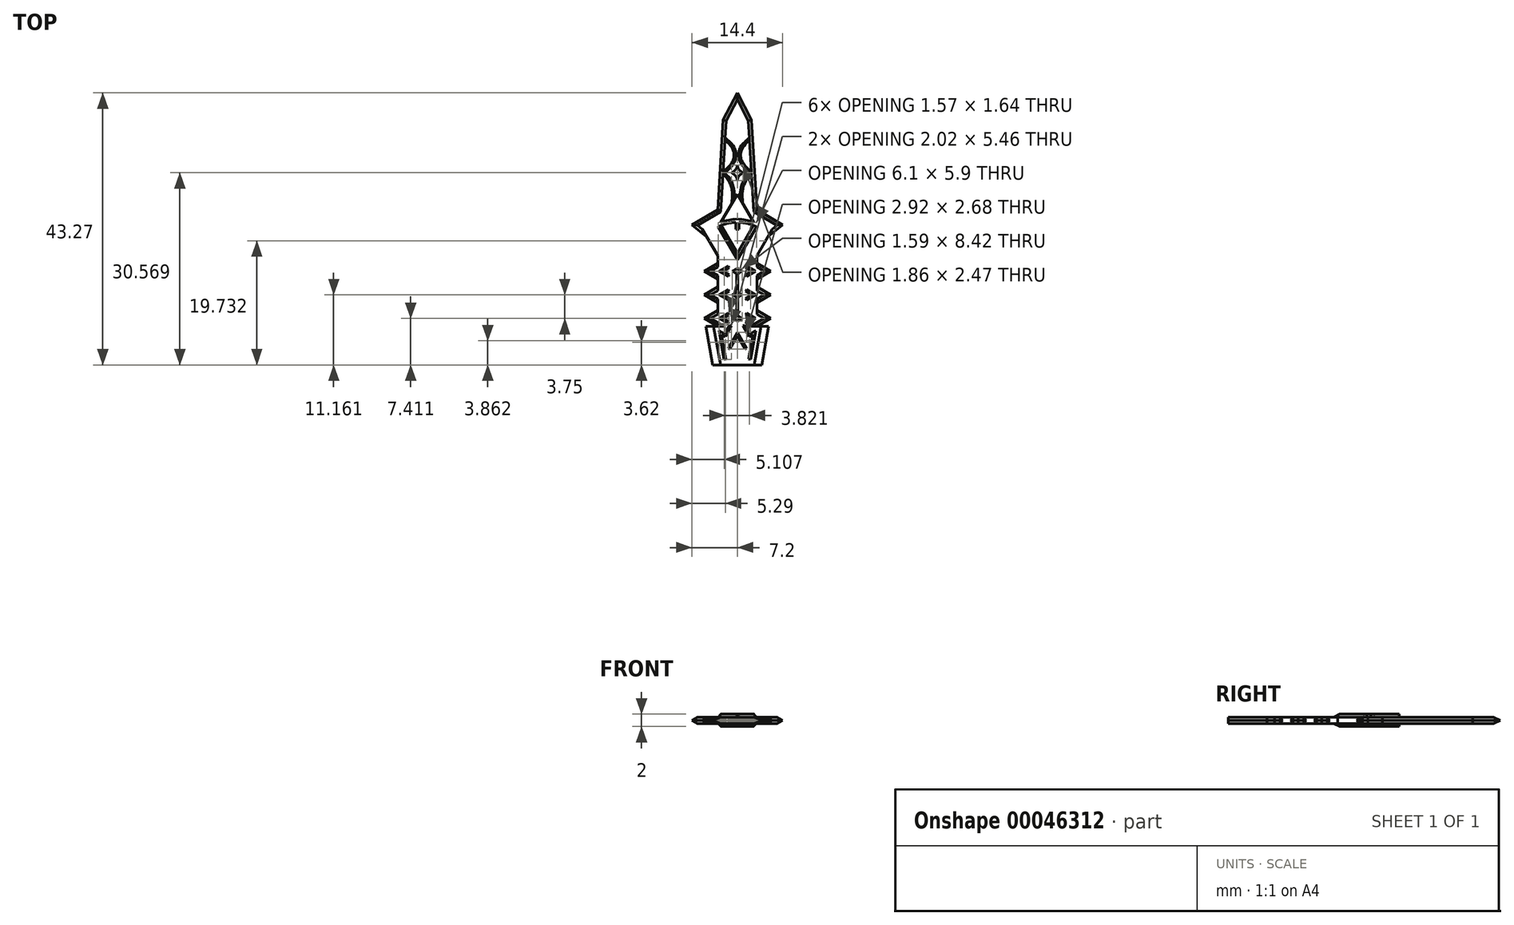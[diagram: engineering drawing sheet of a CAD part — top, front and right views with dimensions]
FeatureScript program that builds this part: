
annotation { "Feature Type Name" : "Feature", "Feature Type Description" : "" }
export const myFeature = defineFeature(function(context is Context, id is Id, definition is map)
    precondition{}
    {
        {
            var Q0;
            Q0=qCreatedBy(makeId("Top.planeOp"),FACE);
            var sketch = newSketch(context, id + "F0", { "sketchPlane" : qUnion([Q0])});
            skLineSegment(sketch, "E0", {"start": v(0, 43.81) * mm, "end": v(-2.25, 39.5) * mm});
            skLineSegment(sketch, "E1", {"start": v(-2.25, 39.5) * mm, "end": v(-3.12, 25.23) * mm});
            skLineSegment(sketch, "E2", {"start": v(-3.12, 25.23) * mm, "end": v(-7.2, 22.8) * mm});
            skLineSegment(sketch, "E3", {"start": v(-7.2, 22.8) * mm, "end": v(-4.87, 20.94) * mm});
            skLineSegment(sketch, "E4", {"start": v(-4.87, 20.94) * mm, "end": v(-3.12, 17.95) * mm});
            skLineSegment(sketch, "E5", {"start": v(-3.12, 17.95) * mm, "end": v(-3.12, 16.7) * mm});
            skLineSegment(sketch, "E6", {"start": v(-3.12, 16.7) * mm, "end": v(-5.28, 15.45) * mm});
            skLineSegment(sketch, "E7", {"start": v(-5.28, 15.45) * mm, "end": v(-3.12, 14.2) * mm});
            skLineSegment(sketch, "E8", {"start": v(-3.12, 14.2) * mm, "end": v(-3.12, 12.95) * mm});
            skLineSegment(sketch, "E9", {"start": v(-3.12, 12.95) * mm, "end": v(-5.28, 11.7) * mm});
            skLineSegment(sketch, "E10", {"start": v(-5.28, 11.7) * mm, "end": v(-3.12, 10.45) * mm});
            skLineSegment(sketch, "E11", {"start": v(-3.12, 10.45) * mm, "end": v(-3.12, 9.2) * mm});
            skLineSegment(sketch, "E12", {"start": v(-3.12, 9.2) * mm, "end": v(-5.28, 7.95) * mm});
            skLineSegment(sketch, "E13", {"start": v(-5.28, 7.95) * mm, "end": v(-3.12, 6.7) * mm});
            skLineSegment(sketch, "E14", {"start": v(-3.12, 6.7) * mm, "end": v(-5.28, 6.7) * mm});
            skLineSegment(sketch, "E15", {"start": v(-5.28, 6.7) * mm, "end": v(-4.2, 0.54) * mm});
            skPoint(sketch, "E15.endSnap0", {"position": v(-4.2, 6.7) * mm});
            skLineSegment(sketch, "E16", {"start": v(-4.2, 0.54) * mm, "end": v(0, 0.54) * mm});
            skLineSegment(sketch, "E17.MirrorCS", {"start": v(3.12, 17.95) * mm, "end": v(3.12, 16.7) * mm});
            skLineSegment(sketch, "E18.MirrorCS", {"start": v(4.87, 20.94) * mm, "end": v(3.12, 17.95) * mm});
            skLineSegment(sketch, "E19.MirrorCS", {"start": v(3.12, 16.7) * mm, "end": v(5.28, 15.45) * mm});
            skLineSegment(sketch, "E20.MirrorCS", {"start": v(5.28, 15.45) * mm, "end": v(3.12, 14.2) * mm});
            skLineSegment(sketch, "E21.MirrorCS", {"start": v(3.12, 14.2) * mm, "end": v(3.12, 12.95) * mm});
            skLineSegment(sketch, "E22.MirrorCS", {"start": v(3.12, 12.95) * mm, "end": v(5.28, 11.7) * mm});
            skLineSegment(sketch, "E23.MirrorCS", {"start": v(5.28, 11.7) * mm, "end": v(3.12, 10.45) * mm});
            skLineSegment(sketch, "E24.MirrorCS", {"start": v(3.12, 10.45) * mm, "end": v(3.12, 9.2) * mm});
            skLineSegment(sketch, "E25.MirrorCS", {"start": v(3.12, 9.2) * mm, "end": v(5.28, 7.95) * mm});
            skLineSegment(sketch, "E26.MirrorCS", {"start": v(5.28, 7.95) * mm, "end": v(3.12, 6.7) * mm});
            skLineSegment(sketch, "E27.MirrorCS", {"start": v(3.12, 6.7) * mm, "end": v(5.28, 6.7) * mm});
            skLineSegment(sketch, "E28.MirrorCS", {"start": v(5.28, 6.7) * mm, "end": v(4.2, 0.54) * mm});
            skLineSegment(sketch, "E29.MirrorCS", {"start": v(0, 43.81) * mm, "end": v(2.25, 39.5) * mm});
            skLineSegment(sketch, "E30.MirrorCS", {"start": v(3.12, 25.23) * mm, "end": v(7.2, 22.8) * mm});
            skLineSegment(sketch, "E31.MirrorCS", {"start": v(7.2, 22.8) * mm, "end": v(4.87, 20.94) * mm});
            skPoint(sketch, "E32.MirrorP", {"position": v(4.2, 6.7) * mm});
            skLineSegment(sketch, "E33.MirrorCS", {"start": v(4.2, 0.54) * mm, "end": v(0, 0.54) * mm});
            skLineSegment(sketch, "E34.MirrorCS", {"start": v(2.25, 39.5) * mm, "end": v(3.12, 25.23) * mm});
            skSolve(sketch);
        }
        {
            var Q0;
            Q0=makeQuery(id+"F0.imprint","IMPRINT",FACE,{"disambiguationData":[TD([[makeQuery(id+"F0.imprint","IMPRINT",EDGE,{"derivedFrom":sQuery(id+"F0.wireOp",EDGE,"E0")}),1.0]])]});
            extrude(context, id + "F1", {"entities" : qUnion([Q0]), "depth" : 0.5 * mm, "hasSecondDirection" : true, "secondDirectionOppositeDirection" : true, "secondDirectionDepth" : 0.5 * mm});
        }
        {
            var Q0;
            Q0=makeQuery(id+"F1.opExtrude","CAP_EDGE",EDGE,{"disambiguationData":[OSD([sQuery(id+"F0.wireOp",EDGE,"E34.MirrorCS")])],"isStart":false});
            var Q1;
            Q1=makeQuery(id+"F1.opExtrude","CAP_EDGE",EDGE,{"disambiguationData":[OSD([sQuery(id+"F0.wireOp",EDGE,"E34.MirrorCS")])],"isStart":true});
            var Q2;
            Q2=makeQuery(id+"F1.opExtrude","CAP_EDGE",EDGE,{"disambiguationData":[OSD([sQuery(id+"F0.wireOp",EDGE,"E29.MirrorCS")])],"isStart":false});
            var Q3;
            Q3=makeQuery(id+"F1.opExtrude","CAP_EDGE",EDGE,{"disambiguationData":[OSD([sQuery(id+"F0.wireOp",EDGE,"E29.MirrorCS")])],"isStart":true});
            var Q4;
            Q4=makeQuery(id+"F1.opExtrude","CAP_EDGE",EDGE,{"disambiguationData":[OSD([sQuery(id+"F0.wireOp",EDGE,"E0")])],"isStart":false});
            var Q5;
            Q5=makeQuery(id+"F1.opExtrude","CAP_EDGE",EDGE,{"disambiguationData":[OSD([sQuery(id+"F0.wireOp",EDGE,"E0")])],"isStart":true});
            var Q6;
            Q6=makeQuery(id+"F1.opExtrude","CAP_EDGE",EDGE,{"disambiguationData":[OSD([sQuery(id+"F0.wireOp",EDGE,"E1")])],"isStart":false});
            var Q7;
            Q7=makeQuery(id+"F1.opExtrude","CAP_EDGE",EDGE,{"disambiguationData":[OSD([sQuery(id+"F0.wireOp",EDGE,"E1")])],"isStart":true});
            var Q8;
            Q8=makeQuery(id+"F1.opExtrude","CAP_EDGE",EDGE,{"disambiguationData":[OSD([sQuery(id+"F0.wireOp",EDGE,"E30.MirrorCS")])],"isStart":true});
            var Q9;
            Q9=makeQuery(id+"F1.opExtrude","CAP_EDGE",EDGE,{"disambiguationData":[OSD([sQuery(id+"F0.wireOp",EDGE,"E30.MirrorCS")])],"isStart":false});
            var Q10;
            Q10=makeQuery(id+"F1.opExtrude","CAP_EDGE",EDGE,{"disambiguationData":[OSD([sQuery(id+"F0.wireOp",EDGE,"E31.MirrorCS")])],"isStart":true});
            var Q11;
            Q11=makeQuery(id+"F1.opExtrude","CAP_EDGE",EDGE,{"disambiguationData":[OSD([sQuery(id+"F0.wireOp",EDGE,"E31.MirrorCS")])],"isStart":false});
            var Q12;
            Q12=makeQuery(id+"F1.opExtrude","CAP_EDGE",EDGE,{"disambiguationData":[OSD([sQuery(id+"F0.wireOp",EDGE,"E2")])],"isStart":false});
            var Q13;
            Q13=makeQuery(id+"F1.opExtrude","CAP_EDGE",EDGE,{"disambiguationData":[OSD([sQuery(id+"F0.wireOp",EDGE,"E2")])],"isStart":true});
            var Q14;
            Q14=makeQuery(id+"F1.opExtrude","CAP_EDGE",EDGE,{"disambiguationData":[OSD([sQuery(id+"F0.wireOp",EDGE,"E3")])],"isStart":false});
            var Q15;
            Q15=makeQuery(id+"F1.opExtrude","CAP_EDGE",EDGE,{"disambiguationData":[OSD([sQuery(id+"F0.wireOp",EDGE,"E3")])],"isStart":true});
            chamfer(context, id + "F2", {"entities" : qUnion([Q0, Q1, Q2, Q3, Q4, Q5, Q6, Q7, Q8, Q9, Q10, Q11, Q12, Q13, Q14, Q15]), "width" : 0.5 * mm, "tangentPropagation" : true});
        }
        {
            var Q0;
            Q0=makeQuery(id+"F1.opExtrude","CAP_EDGE",EDGE,{"disambiguationData":[OSD([sQuery(id+"F0.wireOp",EDGE,"E6")])],"isStart":false});
            var Q1;
            Q1=makeQuery(id+"F1.opExtrude","CAP_EDGE",EDGE,{"disambiguationData":[OSD([sQuery(id+"F0.wireOp",EDGE,"E7")])],"isStart":false});
            var Q2;
            Q2=makeQuery(id+"F1.opExtrude","CAP_EDGE",EDGE,{"disambiguationData":[OSD([sQuery(id+"F0.wireOp",EDGE,"E9")])],"isStart":false});
            var Q3;
            Q3=makeQuery(id+"F1.opExtrude","CAP_EDGE",EDGE,{"disambiguationData":[OSD([sQuery(id+"F0.wireOp",EDGE,"E10")])],"isStart":false});
            var Q4;
            Q4=makeQuery(id+"F1.opExtrude","CAP_EDGE",EDGE,{"disambiguationData":[OSD([sQuery(id+"F0.wireOp",EDGE,"E12")])],"isStart":false});
            var Q5;
            Q5=makeQuery(id+"F1.opExtrude","CAP_EDGE",EDGE,{"disambiguationData":[OSD([sQuery(id+"F0.wireOp",EDGE,"E13")])],"isStart":false});
            var Q6;
            Q6=makeQuery(id+"F1.opExtrude","CAP_EDGE",EDGE,{"disambiguationData":[OSD([sQuery(id+"F0.wireOp",EDGE,"E6")])],"isStart":true});
            var Q7;
            Q7=makeQuery(id+"F1.opExtrude","CAP_EDGE",EDGE,{"disambiguationData":[OSD([sQuery(id+"F0.wireOp",EDGE,"E7")])],"isStart":true});
            var Q8;
            Q8=makeQuery(id+"F1.opExtrude","CAP_EDGE",EDGE,{"disambiguationData":[OSD([sQuery(id+"F0.wireOp",EDGE,"E9")])],"isStart":true});
            var Q9;
            Q9=makeQuery(id+"F1.opExtrude","CAP_EDGE",EDGE,{"disambiguationData":[OSD([sQuery(id+"F0.wireOp",EDGE,"E10")])],"isStart":true});
            var Q10;
            Q10=makeQuery(id+"F1.opExtrude","CAP_EDGE",EDGE,{"disambiguationData":[OSD([sQuery(id+"F0.wireOp",EDGE,"E12")])],"isStart":true});
            var Q11;
            Q11=makeQuery(id+"F1.opExtrude","CAP_EDGE",EDGE,{"disambiguationData":[OSD([sQuery(id+"F0.wireOp",EDGE,"E13")])],"isStart":true});
            var Q12;
            Q12=makeQuery(id+"F1.opExtrude","CAP_EDGE",EDGE,{"disambiguationData":[OSD([sQuery(id+"F0.wireOp",EDGE,"E19.MirrorCS")])],"isStart":true});
            var Q13;
            Q13=makeQuery(id+"F1.opExtrude","CAP_EDGE",EDGE,{"disambiguationData":[OSD([sQuery(id+"F0.wireOp",EDGE,"E19.MirrorCS")])],"isStart":false});
            var Q14;
            Q14=makeQuery(id+"F1.opExtrude","CAP_EDGE",EDGE,{"disambiguationData":[OSD([sQuery(id+"F0.wireOp",EDGE,"E20.MirrorCS")])],"isStart":false});
            var Q15;
            Q15=makeQuery(id+"F1.opExtrude","CAP_EDGE",EDGE,{"disambiguationData":[OSD([sQuery(id+"F0.wireOp",EDGE,"E20.MirrorCS")])],"isStart":true});
            var Q16;
            Q16=makeQuery(id+"F1.opExtrude","CAP_EDGE",EDGE,{"disambiguationData":[OSD([sQuery(id+"F0.wireOp",EDGE,"E22.MirrorCS")])],"isStart":true});
            var Q17;
            Q17=makeQuery(id+"F1.opExtrude","CAP_EDGE",EDGE,{"disambiguationData":[OSD([sQuery(id+"F0.wireOp",EDGE,"E22.MirrorCS")])],"isStart":false});
            var Q18;
            Q18=makeQuery(id+"F1.opExtrude","CAP_EDGE",EDGE,{"disambiguationData":[OSD([sQuery(id+"F0.wireOp",EDGE,"E23.MirrorCS")])],"isStart":false});
            var Q19;
            Q19=makeQuery(id+"F1.opExtrude","CAP_EDGE",EDGE,{"disambiguationData":[OSD([sQuery(id+"F0.wireOp",EDGE,"E23.MirrorCS")])],"isStart":true});
            var Q20;
            Q20=makeQuery(id+"F1.opExtrude","CAP_EDGE",EDGE,{"disambiguationData":[OSD([sQuery(id+"F0.wireOp",EDGE,"E25.MirrorCS")])],"isStart":false});
            var Q21;
            Q21=makeQuery(id+"F1.opExtrude","CAP_EDGE",EDGE,{"disambiguationData":[OSD([sQuery(id+"F0.wireOp",EDGE,"E25.MirrorCS")])],"isStart":true});
            var Q22;
            Q22=makeQuery(id+"F1.opExtrude","CAP_EDGE",EDGE,{"disambiguationData":[OSD([sQuery(id+"F0.wireOp",EDGE,"E26.MirrorCS")])],"isStart":false});
            var Q23;
            Q23=makeQuery(id+"F1.opExtrude","CAP_EDGE",EDGE,{"disambiguationData":[OSD([sQuery(id+"F0.wireOp",EDGE,"E26.MirrorCS")])],"isStart":true});
            chamfer(context, id + "F3", {"entities" : qUnion([Q0, Q1, Q2, Q3, Q4, Q5, Q6, Q7, Q8, Q9, Q10, Q11, Q12, Q13, Q14, Q15, Q16, Q17, Q18, Q19, Q20, Q21, Q22, Q23]), "width" : 0.5 * mm, "tangentPropagation" : true});
        }
        {
            var Q0;
            Q0=makeQuery(id+"F1.opExtrude","CAP_EDGE",EDGE,{"disambiguationData":[OSD([sQuery(id+"F0.wireOp",EDGE,"E15")])],"isStart":false});
            var Q1;
            Q1=makeQuery(id+"F1.opExtrude","CAP_EDGE",EDGE,{"disambiguationData":[OSD([sQuery(id+"F0.wireOp",EDGE,"E15")])],"isStart":true});
            var Q2;
            Q2=makeQuery(id+"F1.opExtrude","CAP_EDGE",EDGE,{"disambiguationData":[OSD([sQuery(id+"F0.wireOp",EDGE,"E28.MirrorCS")])],"isStart":true});
            var Q3;
            Q3=makeQuery(id+"F1.opExtrude","CAP_EDGE",EDGE,{"disambiguationData":[OSD([sQuery(id+"F0.wireOp",EDGE,"E28.MirrorCS")])],"isStart":false});
            chamfer(context, id + "F4", {"entities" : qUnion([Q0, Q1, Q2, Q3]), "chamferType" : ChamferType.OFFSET_ANGLE, "width" : 1.5 * mm, "oppositeDirection" : false, "angle" : 22.5 * degree, "tangentPropagation" : true});
        }
        {
            var Q0;
            Q0=makeQuery(id+"F1.opExtrude","CAP_FACE",FACE,{"disambiguationData":[OSD([sQuery(id+"F0.wireOp",EDGE,"E0"),sQuery(id+"F0.wireOp",EDGE,"E1"),sQuery(id+"F0.wireOp",EDGE,"E2"),sQuery(id+"F0.wireOp",EDGE,"E3"),sQuery(id+"F0.wireOp",EDGE,"E4"),sQuery(id+"F0.wireOp",EDGE,"E5"),sQuery(id+"F0.wireOp",EDGE,"E6"),sQuery(id+"F0.wireOp",EDGE,"E7"),sQuery(id+"F0.wireOp",EDGE,"E8"),sQuery(id+"F0.wireOp",EDGE,"E9"),sQuery(id+"F0.wireOp",EDGE,"E10"),sQuery(id+"F0.wireOp",EDGE,"E11"),sQuery(id+"F0.wireOp",EDGE,"E12"),sQuery(id+"F0.wireOp",EDGE,"E13"),sQuery(id+"F0.wireOp",EDGE,"E14"),sQuery(id+"F0.wireOp",EDGE,"E15"),sQuery(id+"F0.wireOp",EDGE,"E16"),sQuery(id+"F0.wireOp",EDGE,"E17.MirrorCS"),sQuery(id+"F0.wireOp",EDGE,"E18.MirrorCS"),sQuery(id+"F0.wireOp",EDGE,"E19.MirrorCS"),sQuery(id+"F0.wireOp",EDGE,"E20.MirrorCS"),sQuery(id+"F0.wireOp",EDGE,"E21.MirrorCS"),sQuery(id+"F0.wireOp",EDGE,"E22.MirrorCS"),sQuery(id+"F0.wireOp",EDGE,"E23.MirrorCS"),sQuery(id+"F0.wireOp",EDGE,"E24.MirrorCS"),sQuery(id+"F0.wireOp",EDGE,"E25.MirrorCS"),sQuery(id+"F0.wireOp",EDGE,"E26.MirrorCS"),sQuery(id+"F0.wireOp",EDGE,"E27.MirrorCS"),sQuery(id+"F0.wireOp",EDGE,"E28.MirrorCS"),sQuery(id+"F0.wireOp",EDGE,"E29.MirrorCS"),sQuery(id+"F0.wireOp",EDGE,"E30.MirrorCS"),sQuery(id+"F0.wireOp",EDGE,"E31.MirrorCS"),sQuery(id+"F0.wireOp",EDGE,"E33.MirrorCS"),sQuery(id+"F0.wireOp",EDGE,"E34.MirrorCS")])],"isStart":false});
            var sketch = newSketch(context, id + "F5", { "sketchPlane" : qUnion([Q0])});
            skLineSegment(sketch, "E35", {"start": v(-2.11, 1.43) * mm, "end": v(-2.92, 6) * mm});
            skLineSegment(sketch, "E36", {"start": v(-2.92, 6) * mm, "end": v(-1.98, 5.47) * mm});
            skLineSegment(sketch, "E37", {"start": v(-1.98, 5.47) * mm, "end": v(-1.16, 6.89) * mm});
            skLineSegment(sketch, "E38", {"start": v(-1.46, 3.21) * mm, "end": v(0, 5.74) * mm});
            skLineSegment(sketch, "E39.0", {"start": v(-1.87, 5.06) * mm, "end": v(-0.9, 6.74) * mm});
            skLineSegment(sketch, "E39.1", {"start": v(-2.51, 5.42) * mm, "end": v(-1.87, 5.06) * mm});
            skLineSegment(sketch, "E39.2", {"start": v(-1.82, 1.48) * mm, "end": v(-2.51, 5.42) * mm});
            skLineSegment(sketch, "E40.0", {"start": v(-1.2, 3.06) * mm, "end": v(0, 5.14) * mm});
            skLineSegment(sketch, "E41", {"start": v(-1.16, 6.89) * mm, "end": v(-0.9, 6.74) * mm});
            skLineSegment(sketch, "E42", {"start": v(-2.11, 1.43) * mm, "end": v(-1.82, 1.48) * mm});
            skLineSegment(sketch, "E43", {"start": v(-1.46, 3.21) * mm, "end": v(-1.2, 3.06) * mm});
            skLineSegment(sketch, "E44", {"start": v(-1.46, 7.13) * mm, "end": v(-2.88, 7.95) * mm});
            skLineSegment(sketch, "E45", {"start": v(-2.88, 7.95) * mm, "end": v(-1.46, 8.77) * mm});
            skLineSegment(sketch, "E46", {"start": v(-1.46, 10.88) * mm, "end": v(-2.88, 11.7) * mm});
            skLineSegment(sketch, "E47", {"start": v(-2.88, 11.7) * mm, "end": v(-1.46, 12.52) * mm});
            skLineSegment(sketch, "E48", {"start": v(-1.46, 14.63) * mm, "end": v(-2.88, 15.45) * mm});
            skLineSegment(sketch, "E49", {"start": v(-2.88, 15.45) * mm, "end": v(-1.46, 16.27) * mm});
            skLineSegment(sketch, "E50.0", {"start": v(-2.28, 15.45) * mm, "end": v(-1.3, 16.01) * mm});
            skLineSegment(sketch, "E50.1", {"start": v(-1.3, 14.9) * mm, "end": v(-2.28, 15.45) * mm});
            skLineSegment(sketch, "E51.0", {"start": v(-2.28, 11.7) * mm, "end": v(-1.3, 12.26) * mm});
            skLineSegment(sketch, "E51.1", {"start": v(-1.3, 11.14) * mm, "end": v(-2.28, 11.7) * mm});
            skLineSegment(sketch, "E52.0", {"start": v(-2.28, 7.95) * mm, "end": v(-1.3, 8.51) * mm});
            skLineSegment(sketch, "E52.1", {"start": v(-1.3, 7.4) * mm, "end": v(-2.28, 7.95) * mm});
            skLineSegment(sketch, "E53", {"start": v(-1.46, 16.27) * mm, "end": v(-1.3, 16.01) * mm});
            skLineSegment(sketch, "E54", {"start": v(-1.3, 14.9) * mm, "end": v(-1.46, 14.63) * mm});
            skLineSegment(sketch, "E55", {"start": v(-1.46, 12.52) * mm, "end": v(-1.3, 12.26) * mm});
            skLineSegment(sketch, "E56", {"start": v(-1.3, 11.14) * mm, "end": v(-1.46, 10.88) * mm});
            skLineSegment(sketch, "E57", {"start": v(-1.46, 8.77) * mm, "end": v(-1.3, 8.51) * mm});
            skLineSegment(sketch, "E58", {"start": v(-1.3, 7.4) * mm, "end": v(-1.46, 7.13) * mm});
            skLineSegment(sketch, "E59.MirrorCS", {"start": v(1.3, 14.9) * mm, "end": v(1.46, 14.63) * mm});
            skLineSegment(sketch, "E60.MirrorCS", {"start": v(1.3, 7.4) * mm, "end": v(1.46, 7.13) * mm});
            skLineSegment(sketch, "E61.MirrorCS", {"start": v(1.46, 12.52) * mm, "end": v(1.3, 12.26) * mm});
            skLineSegment(sketch, "E62.MirrorCS", {"start": v(1.3, 11.14) * mm, "end": v(1.46, 10.88) * mm});
            skLineSegment(sketch, "E63.MirrorCS", {"start": v(1.46, 16.27) * mm, "end": v(1.3, 16.01) * mm});
            skLineSegment(sketch, "E64.MirrorCS", {"start": v(1.46, 8.77) * mm, "end": v(1.3, 8.51) * mm});
            skLineSegment(sketch, "E65.MirrorCS", {"start": v(2.28, 15.45) * mm, "end": v(1.3, 16.01) * mm});
            skLineSegment(sketch, "E66.MirrorCS", {"start": v(2.28, 7.95) * mm, "end": v(1.3, 8.51) * mm});
            skLineSegment(sketch, "E67.MirrorCS", {"start": v(2.28, 11.7) * mm, "end": v(1.3, 12.26) * mm});
            skLineSegment(sketch, "E68.MirrorCS", {"start": v(1.3, 7.4) * mm, "end": v(2.28, 7.95) * mm});
            skLineSegment(sketch, "E69.MirrorCS", {"start": v(1.3, 14.9) * mm, "end": v(2.28, 15.45) * mm});
            skLineSegment(sketch, "E70.MirrorCS", {"start": v(1.46, 10.88) * mm, "end": v(2.88, 11.7) * mm});
            skLineSegment(sketch, "E71.MirrorCS", {"start": v(1.46, 7.13) * mm, "end": v(2.88, 7.95) * mm});
            skLineSegment(sketch, "E72.MirrorCS", {"start": v(2.88, 7.95) * mm, "end": v(1.46, 8.77) * mm});
            skLineSegment(sketch, "E73.MirrorCS", {"start": v(2.88, 11.7) * mm, "end": v(1.46, 12.52) * mm});
            skLineSegment(sketch, "E74.MirrorCS", {"start": v(1.46, 14.63) * mm, "end": v(2.88, 15.45) * mm});
            skLineSegment(sketch, "E75.MirrorCS", {"start": v(1.3, 11.14) * mm, "end": v(2.28, 11.7) * mm});
            skLineSegment(sketch, "E76.MirrorCS", {"start": v(2.88, 15.45) * mm, "end": v(1.46, 16.27) * mm});
            skLineSegment(sketch, "E77.MirrorCS", {"start": v(1.46, 3.21) * mm, "end": v(1.2, 3.06) * mm});
            skLineSegment(sketch, "E78.MirrorCS", {"start": v(2.11, 1.43) * mm, "end": v(1.82, 1.48) * mm});
            skLineSegment(sketch, "E79.MirrorCS", {"start": v(1.16, 6.89) * mm, "end": v(0.9, 6.74) * mm});
            skLineSegment(sketch, "E80.MirrorCS", {"start": v(2.51, 5.42) * mm, "end": v(1.87, 5.06) * mm});
            skLineSegment(sketch, "E81.MirrorCS", {"start": v(1.98, 5.47) * mm, "end": v(1.16, 6.89) * mm});
            skLineSegment(sketch, "E82.MirrorCS", {"start": v(1.2, 3.06) * mm, "end": v(0, 5.14) * mm});
            skLineSegment(sketch, "E83.MirrorCS", {"start": v(1.87, 5.06) * mm, "end": v(0.9, 6.74) * mm});
            skLineSegment(sketch, "E84.MirrorCS", {"start": v(1.82, 1.48) * mm, "end": v(2.51, 5.42) * mm});
            skLineSegment(sketch, "E85.MirrorCS", {"start": v(2.92, 6) * mm, "end": v(1.98, 5.47) * mm});
            skLineSegment(sketch, "E86.MirrorCS", {"start": v(2.11, 1.43) * mm, "end": v(2.92, 6) * mm});
            skLineSegment(sketch, "E87.MirrorCS", {"start": v(1.46, 3.21) * mm, "end": v(0, 5.74) * mm});
            skLineSegment(sketch, "E88", {"start": v(0, 7.5) * mm, "end": v(-0.8, 7.95) * mm});
            skLineSegment(sketch, "E89", {"start": v(-0.8, 7.95) * mm, "end": v(0, 8.4) * mm});
            skLineSegment(sketch, "E90", {"start": v(0, 12.16) * mm, "end": v(-0.8, 11.7) * mm});
            skLineSegment(sketch, "E91", {"start": v(-0.8, 11.7) * mm, "end": v(0, 11.24) * mm});
            skLineSegment(sketch, "E92", {"start": v(0, 15.9) * mm, "end": v(-0.8, 15.45) * mm});
            skLineSegment(sketch, "E93", {"start": v(-0.8, 15.45) * mm, "end": v(0, 15) * mm});
            skLineSegment(sketch, "E94", {"start": v(-0.1, 15.05) * mm, "end": v(-0.1, 12.1) * mm});
            skLineSegment(sketch, "E95", {"start": v(-0.1, 11.3) * mm, "end": v(-0.1, 8.35) * mm});
            skLineSegment(sketch, "E96.MirrorCS", {"start": v(0, 15.9) * mm, "end": v(0.8, 15.45) * mm});
            skLineSegment(sketch, "E97.MirrorCS", {"start": v(0.8, 15.45) * mm, "end": v(0, 15) * mm});
            skLineSegment(sketch, "E98.MirrorCS", {"start": v(0.1, 15.05) * mm, "end": v(0.1, 12.1) * mm});
            skLineSegment(sketch, "E99.MirrorCS", {"start": v(0, 12.16) * mm, "end": v(0.8, 11.7) * mm});
            skLineSegment(sketch, "E100.MirrorCS", {"start": v(0.8, 11.7) * mm, "end": v(0, 11.24) * mm});
            skLineSegment(sketch, "E101.MirrorCS", {"start": v(0, 7.5) * mm, "end": v(0.8, 7.95) * mm});
            skLineSegment(sketch, "E102.MirrorCS", {"start": v(0.8, 7.95) * mm, "end": v(0, 8.4) * mm});
            skLineSegment(sketch, "E103.MirrorCS", {"start": v(0.1, 11.3) * mm, "end": v(0.1, 8.35) * mm});
            skSolve(sketch);
        }
        {
            var Q0;
            Q0 = qSketchRegion(id + "F5", true);
            extrude(context, id + "F6", {"entities" : qUnion([Q0]), "operationType" : NewBodyOperationType.REMOVE, "oppositeDirection" : true, "depth" : 1 * mm});
        }
        {
            var Q0;
            Q0=qCreatedBy(makeId("Top.planeOp"),FACE);
            var sketch = newSketch(context, id + "F7", { "sketchPlane" : qUnion([Q0])});
            skLineSegment(sketch, "E104", {"start": v(0, 17.32) * mm, "end": v(3.05, 22.53) * mm});
            skLineSegment(sketch, "E105", {"start": v(3.05, 22.53) * mm, "end": v(0, 27.73) * mm});
            skLineSegment(sketch, "E106.MirrorCS", {"start": v(-3.05, 22.53) * mm, "end": v(0, 27.73) * mm});
            skLineSegment(sketch, "E107.MirrorCS", {"start": v(0, 17.32) * mm, "end": v(-3.05, 22.53) * mm});
            skArc(sketch, "E108", {"start": v(3.05, 22.53) * mm, "mid": v(0, 23.23) * mm, "end": v(-3.05, 22.53) * mm});
            skArc(sketch, "E109", {"start": v(2.64, 23.23) * mm, "mid": v(0, 23.74) * mm, "end": v(-2.64, 23.23) * mm});
            skPoint(sketch, "E109.startSnap0", {"position": v(0, 23.23) * mm});
            skLineSegment(sketch, "E110", {"start": v(0, 23.74) * mm, "end": v(0, 23.23) * mm, "construction": true});
            skLineSegment(sketch, "E111", {"start": v(0, 16.74) * mm, "end": v(0, 16.22) * mm, "construction": true});
            skLineSegment(sketch, "E112", {"start": v(-0.24, 23.22) * mm, "end": v(-0.24, 22.12) * mm});
            skLineSegment(sketch, "E113", {"start": v(-0.24, 22.12) * mm, "end": v(0, 22.12) * mm});
            skLineSegment(sketch, "E114.MirrorCS", {"start": v(0.24, 23.22) * mm, "end": v(0.24, 22.12) * mm});
            skLineSegment(sketch, "E115.MirrorCS", {"start": v(0.24, 22.12) * mm, "end": v(0, 22.12) * mm});
            skSolve(sketch);
        }
        {
            var Q0;
            {var subQ0=sQuery(id+"F7.wireOp",EDGE,"E109");Q0=makeQuery(id+"F7.imprint","IMPRINT",FACE,{"disambiguationData":[TD([[makeQuery(id+"F7.imprint","IMPRINT",EDGE,{"derivedFrom":subQ0}),-1.0]])]});}
            var Q1;
            {var subQ1=sQuery(id+"F7.wireOp",EDGE,"E104");Q1=makeQuery(id+"F7.imprint","IMPRINT",FACE,{"disambiguationData":[TD([[makeQuery(id+"F7.imprint","IMPRINT",EDGE,{"derivedFrom":subQ1}),1.0]])]});}
            extrude(context, id + "F8", {"entities" : qUnion([Q0, Q1]), "operationType" : NewBodyOperationType.ADD, "depth" : 1 * mm, "hasSecondDirection" : true, "secondDirectionOppositeDirection" : true, "secondDirectionDepth" : 1 * mm});
        }
        {
            var Q0;
            Q0=makeQuery(id+"F8.opExtrude","CAP_EDGE",EDGE,{"disambiguationData":[OSD([sQuery(id+"F7.wireOp",EDGE,"E104")])],"isStart":false});
            var Q1;
            Q1=makeQuery(id+"F8.opExtrude","CAP_EDGE",EDGE,{"disambiguationData":[OSD([sQuery(id+"F7.wireOp",EDGE,"E107.MirrorCS")])],"isStart":false});
            var Q2;
            Q2=makeQuery(id+"F8.opExtrude","CAP_EDGE",EDGE,{"disambiguationData":[OSD([sQuery(id+"F7.wireOp",EDGE,"E107.MirrorCS")])],"isStart":true});
            var Q3;
            Q3=makeQuery(id+"F8.opExtrude","CAP_EDGE",EDGE,{"disambiguationData":[OSD([sQuery(id+"F7.wireOp",EDGE,"E104")])],"isStart":true});
            chamfer(context, id + "F9", {"entities" : qUnion([Q0, Q1, Q2, Q3]), "width" : 0.5 * mm, "tangentPropagation" : true});
        }
        {
            var Q0;
            Q0=makeQuery(id+"F1.opExtrude","CAP_FACE",FACE,{"disambiguationData":[OSD([sQuery(id+"F0.wireOp",EDGE,"E0"),sQuery(id+"F0.wireOp",EDGE,"E1"),sQuery(id+"F0.wireOp",EDGE,"E2"),sQuery(id+"F0.wireOp",EDGE,"E3"),sQuery(id+"F0.wireOp",EDGE,"E4"),sQuery(id+"F0.wireOp",EDGE,"E5"),sQuery(id+"F0.wireOp",EDGE,"E6"),sQuery(id+"F0.wireOp",EDGE,"E7"),sQuery(id+"F0.wireOp",EDGE,"E8"),sQuery(id+"F0.wireOp",EDGE,"E9"),sQuery(id+"F0.wireOp",EDGE,"E10"),sQuery(id+"F0.wireOp",EDGE,"E11"),sQuery(id+"F0.wireOp",EDGE,"E12"),sQuery(id+"F0.wireOp",EDGE,"E13"),sQuery(id+"F0.wireOp",EDGE,"E14"),sQuery(id+"F0.wireOp",EDGE,"E15"),sQuery(id+"F0.wireOp",EDGE,"E16"),sQuery(id+"F0.wireOp",EDGE,"E17.MirrorCS"),sQuery(id+"F0.wireOp",EDGE,"E18.MirrorCS"),sQuery(id+"F0.wireOp",EDGE,"E19.MirrorCS"),sQuery(id+"F0.wireOp",EDGE,"E20.MirrorCS"),sQuery(id+"F0.wireOp",EDGE,"E21.MirrorCS"),sQuery(id+"F0.wireOp",EDGE,"E22.MirrorCS"),sQuery(id+"F0.wireOp",EDGE,"E23.MirrorCS"),sQuery(id+"F0.wireOp",EDGE,"E24.MirrorCS"),sQuery(id+"F0.wireOp",EDGE,"E25.MirrorCS"),sQuery(id+"F0.wireOp",EDGE,"E26.MirrorCS"),sQuery(id+"F0.wireOp",EDGE,"E27.MirrorCS"),sQuery(id+"F0.wireOp",EDGE,"E28.MirrorCS"),sQuery(id+"F0.wireOp",EDGE,"E29.MirrorCS"),sQuery(id+"F0.wireOp",EDGE,"E30.MirrorCS"),sQuery(id+"F0.wireOp",EDGE,"E31.MirrorCS"),sQuery(id+"F0.wireOp",EDGE,"E33.MirrorCS"),sQuery(id+"F0.wireOp",EDGE,"E34.MirrorCS")])],"isStart":false});
            var sketch = newSketch(context, id + "F10", { "sketchPlane" : qUnion([Q0])});
            skFitSpline(sketch, "E116", {"points": [v(-0.9, 26.19) * mm, v(-0.9, 28.6) * mm, v(-2.27, 30.92) * mm], "startDerivative": vector(0.78, 5.68) * mm, "endDerivative": vector(-4.27, 3.98) * mm});
            skFitSpline(sketch, "E117", {"points": [v(-2.25, 31.32) * mm, v(-0.95, 32.62) * mm, v(-0.53, 33.9) * mm, v(-1.95, 36.28) * mm], "startDerivative": vector(4.53, 3.32) * mm, "endDerivative": vector(-8.52, 6.9) * mm});
            skFitSpline(sketch, "E118.0", {"points": [v(-0.6, 26.14) * mm, v(-0.54, 26.62) * mm, v(-0.47, 27.28) * mm, v(-0.5, 28.11) * mm, v(-0.64, 28.95) * mm, v(-1.07, 30.01) * mm, v(-1.69, 30.8) * mm, v(-2.07, 31.14) * mm]});
            skLineSegment(sketch, "E119", {"start": v(-0.52, 26.84) * mm, "end": v(-0.9, 26.19) * mm});
            skLineSegment(sketch, "E120", {"start": v(-2.25, 31.32) * mm, "end": v(-2.27, 30.92) * mm});
            skLineSegment(sketch, "E121", {"start": v(-1.93, 36.58) * mm, "end": v(-1.95, 36.28) * mm});
            skLineSegment(sketch, "E122.MirrorCS", {"start": v(2.25, 31.32) * mm, "end": v(2.27, 30.92) * mm});
            skLineSegment(sketch, "E123.MirrorCS", {"start": v(1.93, 36.58) * mm, "end": v(1.95, 36.28) * mm});
            skFitSpline(sketch, "E124.MirrorCS", {"points": [v(0.9, 26.19) * mm, v(0.9, 28.6) * mm, v(2.27, 30.92) * mm], "startDerivative": vector(-0.78, 5.68) * mm, "endDerivative": vector(4.27, 3.98) * mm});
            skFitSpline(sketch, "E125.MirrorCS", {"points": [v(2.25, 31.32) * mm, v(0.95, 32.62) * mm, v(0.53, 33.9) * mm, v(1.95, 36.28) * mm], "startDerivative": vector(-4.53, 3.32) * mm, "endDerivative": vector(8.52, 6.9) * mm});
            skLineSegment(sketch, "E126.MirrorCS", {"start": v(0.52, 26.84) * mm, "end": v(0.9, 26.19) * mm});
            skFitSpline(sketch, "E127.0", {"points": [v(-2.07, 31.08) * mm, v(-1.87, 31.22) * mm, v(-1.48, 31.55) * mm, v(-0.94, 32.1) * mm, v(-0.53, 32.7) * mm, v(-0.31, 33.22) * mm, v(-0.23, 33.67) * mm, v(-0.22, 34.15) * mm, v(-0.34, 34.8) * mm, v(-0.81, 35.63) * mm, v(-1.39, 36.22) * mm, v(-1.76, 36.51) * mm]});
            skLineSegment(sketch, "E128", {"start": v(-1.76, 36.51) * mm, "end": v(-1.93, 36.58) * mm});
            skLineSegment(sketch, "E129.MirrorCS", {"start": v(1.76, 36.51) * mm, "end": v(1.93, 36.58) * mm});
            skFitSpline(sketch, "E130.0", {"points": [v(0.6, 26.14) * mm, v(0.54, 26.62) * mm, v(0.47, 27.28) * mm, v(0.5, 28.11) * mm, v(0.64, 28.95) * mm, v(1.07, 30.01) * mm, v(1.69, 30.8) * mm, v(2.07, 31.14) * mm]});
            skFitSpline(sketch, "E131.0", {"points": [v(2.07, 31.08) * mm, v(1.87, 31.22) * mm, v(1.48, 31.55) * mm, v(0.94, 32.1) * mm, v(0.53, 32.7) * mm, v(0.31, 33.22) * mm, v(0.23, 33.67) * mm, v(0.22, 34.15) * mm, v(0.34, 34.8) * mm, v(0.81, 35.63) * mm, v(1.39, 36.22) * mm, v(1.76, 36.51) * mm]});
            skArc(sketch, "E132", {"start": v(-0.93, 31.1) * mm, "mid": v(-0.3, 31.6) * mm, "end": v(0, 32.35) * mm});
            skArc(sketch, "E133.MirrorCS", {"start": v(0.93, 31.1) * mm, "mid": v(0.3, 31.6) * mm, "end": v(0, 32.35) * mm});
            skLineSegment(sketch, "E134", {"start": v(-0.93, 31.1) * mm, "end": v(0.93, 31.1) * mm, "construction": true});
            skArc(sketch, "E135.MirrorCS", {"start": v(0.93, 31.1) * mm, "mid": v(0.3, 30.62) * mm, "end": v(0, 29.87) * mm});
            skArc(sketch, "E136.MirrorCS", {"start": v(-0.93, 31.1) * mm, "mid": v(-0.3, 30.62) * mm, "end": v(0, 29.87) * mm});
            skSolve(sketch);
        }
        {
            var Q0;
            Q0=makeQuery(id+"F10.imprint","IMPRINT",FACE,{"disambiguationData":[TD([[makeQuery(id+"F10.imprint","IMPRINT",EDGE,{"derivedFrom":sQuery(id+"F10.wireOp",EDGE,"E122.MirrorCS")}),1.0]])]});
            var Q1;
            Q1=makeQuery(id+"F10.imprint","IMPRINT",FACE,{"disambiguationData":[TD([[makeQuery(id+"F10.imprint","IMPRINT",EDGE,{"derivedFrom":sQuery(id+"F10.wireOp",EDGE,"E116")}),-1.0]])]});
            var Q2;
            Q2=makeQuery(id+"F10.imprint","IMPRINT",FACE,{"disambiguationData":[TD([[makeQuery(id+"F10.imprint","IMPRINT",EDGE,{"derivedFrom":sQuery(id+"F10.wireOp",EDGE,"E132")}),-1.0]])]});
            extrude(context, id + "F11", {"entities" : qUnion([Q0, Q1, Q2]), "operationType" : NewBodyOperationType.REMOVE, "flatOperationType" : FlatOperationType.REMOVE, "oppositeDirection" : true, "offsetDistance" : 25 * mm, "depth" : 1 * mm, "domain" : OperationDomain.MODEL});
        }
    });
